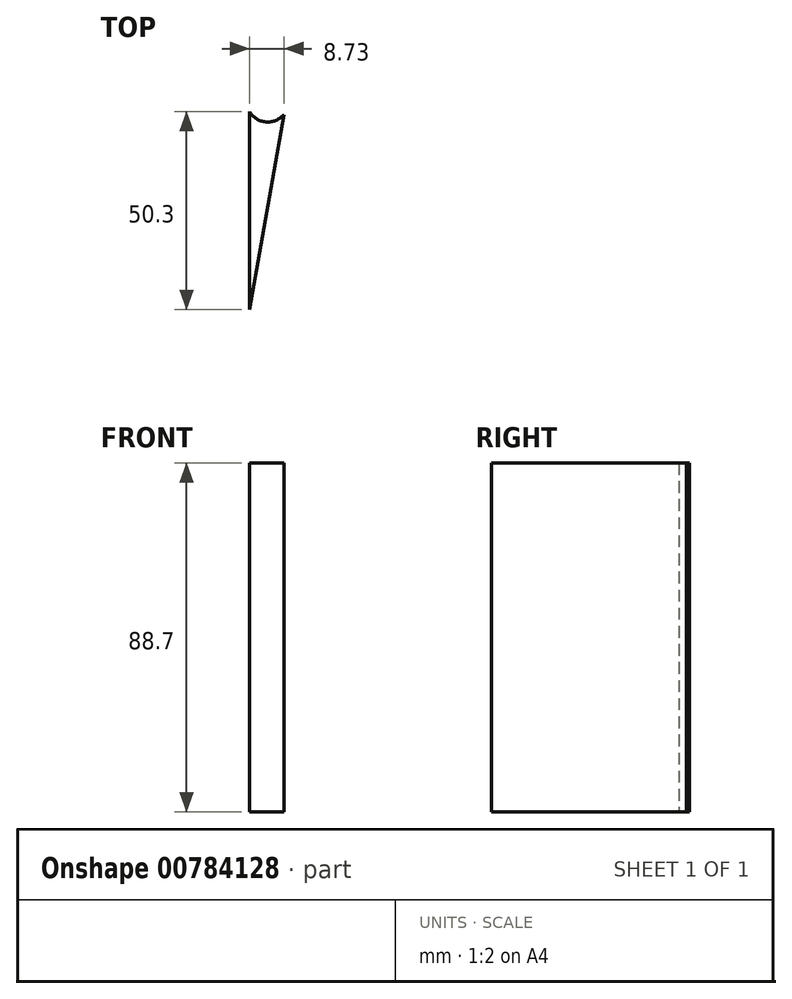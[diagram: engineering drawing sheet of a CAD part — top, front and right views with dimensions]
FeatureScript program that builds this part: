
annotation { "Feature Type Name" : "Feature", "Feature Type Description" : "" }
export const myFeature = defineFeature(function(context is Context, id is Id, definition is map)
    precondition{}
    {
        {
            var Q0;
            Q0=qCreatedBy(makeId("Top.planeOp"),FACE);
            var sketch = newSketch(context, id + "F0", { "sketchPlane" : qUnion([Q0])});
            skArc(sketch, "E0", {"start": v(0, 50.3) * mm, "mid": v(4.17, 47.65) * mm, "end": v(8.73, 49.53) * mm});
            skLineSegment(sketch, "E1", {"start": v(0, 50.3) * mm, "end": v(0, 0) * mm});
            skLineSegment(sketch, "E2", {"start": v(0, 0) * mm, "end": v(8.73, 49.53) * mm});
            skSolve(sketch);
        }
        {
            var Q0;
            Q0=qCreatedBy(makeId("Front.planeOp"),FACE);
            var sketch = newSketch(context, id + "F1", { "sketchPlane" : qUnion([Q0])});
            skLineSegment(sketch, "E3", {"start": v(0, 0) * mm, "end": v(0, 40.63) * mm});
            skSolve(sketch);
        }
        {
            var Q0;
            Q0=makeQuery(id+"FnWcQ6zkBOcur6w_0.24.F0.imprint","IMPRINT",FACE,{"disambiguationData":[TD([[makeQuery(id+"FnWcQ6zkBOcur6w_0.24.F0.imprint","IMPRINT",EDGE,{"derivedFrom":sQuery(id+"FnWcQ6zkBOcur6w_0.24.F0.wireOp",EDGE,"E0")}),-1.0]])]});
            var Q1;
            Q1=makeQuery(id+"FnWcQ6zkBOcur6w_0.16.F0.imprint","IMPRINT",FACE,{"disambiguationData":[TD([[makeQuery(id+"FnWcQ6zkBOcur6w_0.16.F0.imprint","IMPRINT",EDGE,{"derivedFrom":sQuery(id+"FnWcQ6zkBOcur6w_0.16.F0.wireOp",EDGE,"E0")}),-1.0]])]});
            var Q2;
            Q2=makeQuery(id+"FnWcQ6zkBOcur6w_0.19.F0.imprint","IMPRINT",FACE,{"disambiguationData":[TD([[makeQuery(id+"FnWcQ6zkBOcur6w_0.19.F0.imprint","IMPRINT",EDGE,{"derivedFrom":sQuery(id+"FnWcQ6zkBOcur6w_0.19.F0.wireOp",EDGE,"E0")}),-1.0]])]});
            var Q3;
            Q3=makeQuery(id+"FnWcQ6zkBOcur6w_0.-10.F0.imprint","IMPRINT",FACE,{"disambiguationData":[TD([[makeQuery(id+"FnWcQ6zkBOcur6w_0.-10.F0.imprint","IMPRINT",EDGE,{"derivedFrom":sQuery(id+"FnWcQ6zkBOcur6w_0.-10.F0.wireOp",EDGE,"E0")}),-1.0]])]});
            var Q4;
            Q4=makeQuery(id+"FnWcQ6zkBOcur6w_0.11.F0.imprint","IMPRINT",FACE,{"disambiguationData":[TD([[makeQuery(id+"FnWcQ6zkBOcur6w_0.11.F0.imprint","IMPRINT",EDGE,{"derivedFrom":sQuery(id+"FnWcQ6zkBOcur6w_0.11.F0.wireOp",EDGE,"E0")}),-1.0]])]});
            var Q5;
            Q5=makeQuery(id+"FnWcQ6zkBOcur6w_0.-20.F0.imprint","IMPRINT",FACE,{"disambiguationData":[TD([[makeQuery(id+"FnWcQ6zkBOcur6w_0.-20.F0.imprint","IMPRINT",EDGE,{"derivedFrom":sQuery(id+"FnWcQ6zkBOcur6w_0.-20.F0.wireOp",EDGE,"E0")}),-1.0]])]});
            var Q6;
            Q6=makeQuery(id+"FnWcQ6zkBOcur6w_0.-13.F0.imprint","IMPRINT",FACE,{"disambiguationData":[TD([[makeQuery(id+"FnWcQ6zkBOcur6w_0.-13.F0.imprint","IMPRINT",EDGE,{"derivedFrom":sQuery(id+"FnWcQ6zkBOcur6w_0.-13.F0.wireOp",EDGE,"E0")}),-1.0]])]});
            var Q7;
            Q7=makeQuery(id+"FnWcQ6zkBOcur6w_0.-17.F0.imprint","IMPRINT",FACE,{"disambiguationData":[TD([[makeQuery(id+"FnWcQ6zkBOcur6w_0.-17.F0.imprint","IMPRINT",EDGE,{"derivedFrom":sQuery(id+"FnWcQ6zkBOcur6w_0.-17.F0.wireOp",EDGE,"E0")}),-1.0]])]});
            var Q8;
            Q8=makeQuery(id+"FnWcQ6zkBOcur6w_0.-8.F0.imprint","IMPRINT",FACE,{"disambiguationData":[TD([[makeQuery(id+"FnWcQ6zkBOcur6w_0.-8.F0.imprint","IMPRINT",EDGE,{"derivedFrom":sQuery(id+"FnWcQ6zkBOcur6w_0.-8.F0.wireOp",EDGE,"E0")}),-1.0]])]});
            var Q9;
            Q9=makeQuery(id+"FnWcQ6zkBOcur6w_0.20.F0.imprint","IMPRINT",FACE,{"disambiguationData":[TD([[makeQuery(id+"FnWcQ6zkBOcur6w_0.20.F0.imprint","IMPRINT",EDGE,{"derivedFrom":sQuery(id+"FnWcQ6zkBOcur6w_0.20.F0.wireOp",EDGE,"E0")}),-1.0]])]});
            var Q10;
            Q10=makeQuery(id+"FnWcQ6zkBOcur6w_0.-16.F0.imprint","IMPRINT",FACE,{"disambiguationData":[TD([[makeQuery(id+"FnWcQ6zkBOcur6w_0.-16.F0.imprint","IMPRINT",EDGE,{"derivedFrom":sQuery(id+"FnWcQ6zkBOcur6w_0.-16.F0.wireOp",EDGE,"E0")}),-1.0]])]});
            var Q11;
            Q11=makeQuery(id+"FnWcQ6zkBOcur6w_0.12.F0.imprint","IMPRINT",FACE,{"disambiguationData":[TD([[makeQuery(id+"FnWcQ6zkBOcur6w_0.12.F0.imprint","IMPRINT",EDGE,{"derivedFrom":sQuery(id+"FnWcQ6zkBOcur6w_0.12.F0.wireOp",EDGE,"E0")}),-1.0]])]});
            var Q12;
            Q12=makeQuery(id+"FnWcQ6zkBOcur6w_0.25.F0.imprint","IMPRINT",FACE,{"disambiguationData":[TD([[makeQuery(id+"FnWcQ6zkBOcur6w_0.25.F0.imprint","IMPRINT",EDGE,{"derivedFrom":sQuery(id+"FnWcQ6zkBOcur6w_0.25.F0.wireOp",EDGE,"E0")}),-1.0]])]});
            var Q13;
            Q13=makeQuery(id+"FnWcQ6zkBOcur6w_0.-9.F0.imprint","IMPRINT",FACE,{"disambiguationData":[TD([[makeQuery(id+"FnWcQ6zkBOcur6w_0.-9.F0.imprint","IMPRINT",EDGE,{"derivedFrom":sQuery(id+"FnWcQ6zkBOcur6w_0.-9.F0.wireOp",EDGE,"E0")}),-1.0]])]});
            var Q14;
            Q14=makeQuery(id+"FnWcQ6zkBOcur6w_0.-12.F0.imprint","IMPRINT",FACE,{"disambiguationData":[TD([[makeQuery(id+"FnWcQ6zkBOcur6w_0.-12.F0.imprint","IMPRINT",EDGE,{"derivedFrom":sQuery(id+"FnWcQ6zkBOcur6w_0.-12.F0.wireOp",EDGE,"E0")}),-1.0]])]});
            var Q15;
            Q15=makeQuery(id+"FnWcQ6zkBOcur6w_0.-15.F0.imprint","IMPRINT",FACE,{"disambiguationData":[TD([[makeQuery(id+"FnWcQ6zkBOcur6w_0.-15.F0.imprint","IMPRINT",EDGE,{"derivedFrom":sQuery(id+"FnWcQ6zkBOcur6w_0.-15.F0.wireOp",EDGE,"E0")}),-1.0]])]});
            var Q16;
            Q16=makeQuery(id+"FnWcQ6zkBOcur6w_0.13.F0.imprint","IMPRINT",FACE,{"disambiguationData":[TD([[makeQuery(id+"FnWcQ6zkBOcur6w_0.13.F0.imprint","IMPRINT",EDGE,{"derivedFrom":sQuery(id+"FnWcQ6zkBOcur6w_0.13.F0.wireOp",EDGE,"E0")}),-1.0]])]});
            var Q17;
            Q17=makeQuery(id+"FnWcQ6zkBOcur6w_0.26.F0.imprint","IMPRINT",FACE,{"disambiguationData":[TD([[makeQuery(id+"FnWcQ6zkBOcur6w_0.26.F0.imprint","IMPRINT",EDGE,{"derivedFrom":sQuery(id+"FnWcQ6zkBOcur6w_0.26.F0.wireOp",EDGE,"E0")}),-1.0]])]});
            var Q18;
            Q18=makeQuery(id+"FnWcQ6zkBOcur6w_0.-21.F0.imprint","IMPRINT",FACE,{"disambiguationData":[TD([[makeQuery(id+"FnWcQ6zkBOcur6w_0.-21.F0.imprint","IMPRINT",EDGE,{"derivedFrom":sQuery(id+"FnWcQ6zkBOcur6w_0.-21.F0.wireOp",EDGE,"E0")}),-1.0]])]});
            var Q19;
            Q19=makeQuery(id+"FnWcQ6zkBOcur6w_0.-22.F0.imprint","IMPRINT",FACE,{"disambiguationData":[TD([[makeQuery(id+"FnWcQ6zkBOcur6w_0.-22.F0.imprint","IMPRINT",EDGE,{"derivedFrom":sQuery(id+"FnWcQ6zkBOcur6w_0.-22.F0.wireOp",EDGE,"E0")}),-1.0]])]});
            var Q20;
            Q20=makeQuery(id+"FnWcQ6zkBOcur6w_0.18.F0.imprint","IMPRINT",FACE,{"disambiguationData":[TD([[makeQuery(id+"FnWcQ6zkBOcur6w_0.18.F0.imprint","IMPRINT",EDGE,{"derivedFrom":sQuery(id+"FnWcQ6zkBOcur6w_0.18.F0.wireOp",EDGE,"E0")}),-1.0]])]});
            var Q21;
            Q21=makeQuery(id+"FnWcQ6zkBOcur6w_0.-23.F0.imprint","IMPRINT",FACE,{"disambiguationData":[TD([[makeQuery(id+"FnWcQ6zkBOcur6w_0.-23.F0.imprint","IMPRINT",EDGE,{"derivedFrom":sQuery(id+"FnWcQ6zkBOcur6w_0.-23.F0.wireOp",EDGE,"E0")}),-1.0]])]});
            var Q22;
            Q22=makeQuery(id+"FnWcQ6zkBOcur6w_0.-24.F0.imprint","IMPRINT",FACE,{"disambiguationData":[TD([[makeQuery(id+"FnWcQ6zkBOcur6w_0.-24.F0.imprint","IMPRINT",EDGE,{"derivedFrom":sQuery(id+"FnWcQ6zkBOcur6w_0.-24.F0.wireOp",EDGE,"E0")}),-1.0]])]});
            var Q23;
            Q23=makeQuery(id+"FnWcQ6zkBOcur6w_0.10.F0.imprint","IMPRINT",FACE,{"disambiguationData":[TD([[makeQuery(id+"FnWcQ6zkBOcur6w_0.10.F0.imprint","IMPRINT",EDGE,{"derivedFrom":sQuery(id+"FnWcQ6zkBOcur6w_0.10.F0.wireOp",EDGE,"E0")}),-1.0]])]});
            var Q24;
            Q24=makeQuery(id+"FnWcQ6zkBOcur6w_0.-25.F0.imprint","IMPRINT",FACE,{"disambiguationData":[TD([[makeQuery(id+"FnWcQ6zkBOcur6w_0.-25.F0.imprint","IMPRINT",EDGE,{"derivedFrom":sQuery(id+"FnWcQ6zkBOcur6w_0.-25.F0.wireOp",EDGE,"E0")}),-1.0]])]});
            var Q25;
            Q25=makeQuery(id+"FnWcQ6zkBOcur6w_0.-26.F0.imprint","IMPRINT",FACE,{"disambiguationData":[TD([[makeQuery(id+"FnWcQ6zkBOcur6w_0.-26.F0.imprint","IMPRINT",EDGE,{"derivedFrom":sQuery(id+"FnWcQ6zkBOcur6w_0.-26.F0.wireOp",EDGE,"E0")}),-1.0]])]});
            var Q26;
            Q26=makeQuery(id+"FnWcQ6zkBOcur6w_0.23.F0.imprint","IMPRINT",FACE,{"disambiguationData":[TD([[makeQuery(id+"FnWcQ6zkBOcur6w_0.23.F0.imprint","IMPRINT",EDGE,{"derivedFrom":sQuery(id+"FnWcQ6zkBOcur6w_0.23.F0.wireOp",EDGE,"E0")}),-1.0]])]});
            var Q27;
            Q27=makeQuery(id+"FnWcQ6zkBOcur6w_0.27.F0.imprint","IMPRINT",FACE,{"disambiguationData":[TD([[makeQuery(id+"FnWcQ6zkBOcur6w_0.27.F0.imprint","IMPRINT",EDGE,{"derivedFrom":sQuery(id+"FnWcQ6zkBOcur6w_0.27.F0.wireOp",EDGE,"E0")}),-1.0]])]});
            var Q28;
            Q28=makeQuery(id+"FnWcQ6zkBOcur6w_0.-11.F0.imprint","IMPRINT",FACE,{"disambiguationData":[TD([[makeQuery(id+"FnWcQ6zkBOcur6w_0.-11.F0.imprint","IMPRINT",EDGE,{"derivedFrom":sQuery(id+"FnWcQ6zkBOcur6w_0.-11.F0.wireOp",EDGE,"E0")}),-1.0]])]});
            var Q29;
            Q29=makeQuery(id+"FnWcQ6zkBOcur6w_0.15.F0.imprint","IMPRINT",FACE,{"disambiguationData":[TD([[makeQuery(id+"FnWcQ6zkBOcur6w_0.15.F0.imprint","IMPRINT",EDGE,{"derivedFrom":sQuery(id+"FnWcQ6zkBOcur6w_0.15.F0.wireOp",EDGE,"E0")}),-1.0]])]});
            var Q30;
            Q30=makeQuery(id+"FnWcQ6zkBOcur6w_0.-14.F0.imprint","IMPRINT",FACE,{"disambiguationData":[TD([[makeQuery(id+"FnWcQ6zkBOcur6w_0.-14.F0.imprint","IMPRINT",EDGE,{"derivedFrom":sQuery(id+"FnWcQ6zkBOcur6w_0.-14.F0.wireOp",EDGE,"E0")}),-1.0]])]});
            var Q31;
            Q31=makeQuery(id+"FnWcQ6zkBOcur6w_0.14.F0.imprint","IMPRINT",FACE,{"disambiguationData":[TD([[makeQuery(id+"FnWcQ6zkBOcur6w_0.14.F0.imprint","IMPRINT",EDGE,{"derivedFrom":sQuery(id+"FnWcQ6zkBOcur6w_0.14.F0.wireOp",EDGE,"E0")}),-1.0]])]});
            var Q32;
            Q32=makeQuery(id+"FnWcQ6zkBOcur6w_0.-18.F0.imprint","IMPRINT",FACE,{"disambiguationData":[TD([[makeQuery(id+"FnWcQ6zkBOcur6w_0.-18.F0.imprint","IMPRINT",EDGE,{"derivedFrom":sQuery(id+"FnWcQ6zkBOcur6w_0.-18.F0.wireOp",EDGE,"E0")}),-1.0]])]});
            var Q33;
            Q33=makeQuery(id+"FnWcQ6zkBOcur6w_0.28.F0.imprint","IMPRINT",FACE,{"disambiguationData":[TD([[makeQuery(id+"FnWcQ6zkBOcur6w_0.28.F0.imprint","IMPRINT",EDGE,{"derivedFrom":sQuery(id+"FnWcQ6zkBOcur6w_0.28.F0.wireOp",EDGE,"E0")}),-1.0]])]});
            var Q34;
            Q34=makeQuery(id+"FnWcQ6zkBOcur6w_0.4.F0.imprint","IMPRINT",FACE,{"disambiguationData":[TD([[makeQuery(id+"FnWcQ6zkBOcur6w_0.4.F0.imprint","IMPRINT",EDGE,{"derivedFrom":sQuery(id+"FnWcQ6zkBOcur6w_0.4.F0.wireOp",EDGE,"E0")}),-1.0]])]});
            var Q35;
            Q35=makeQuery(id+"FnWcQ6zkBOcur6w_0.-33.F0.imprint","IMPRINT",FACE,{"disambiguationData":[TD([[makeQuery(id+"FnWcQ6zkBOcur6w_0.-33.F0.imprint","IMPRINT",EDGE,{"derivedFrom":sQuery(id+"FnWcQ6zkBOcur6w_0.-33.F0.wireOp",EDGE,"E0")}),-1.0]])]});
            var Q36;
            Q36=makeQuery(id+"FnWcQ6zkBOcur6w_0.-2.F0.imprint","IMPRINT",FACE,{"disambiguationData":[TD([[makeQuery(id+"FnWcQ6zkBOcur6w_0.-2.F0.imprint","IMPRINT",EDGE,{"derivedFrom":sQuery(id+"FnWcQ6zkBOcur6w_0.-2.F0.wireOp",EDGE,"E0")}),-1.0]])]});
            var Q37;
            Q37=makeQuery(id+"FnWcQ6zkBOcur6w_0.35.F0.imprint","IMPRINT",FACE,{"disambiguationData":[TD([[makeQuery(id+"FnWcQ6zkBOcur6w_0.35.F0.imprint","IMPRINT",EDGE,{"derivedFrom":sQuery(id+"FnWcQ6zkBOcur6w_0.35.F0.wireOp",EDGE,"E0")}),-1.0]])]});
            var Q38;
            Q38=makeQuery(id+"FnWcQ6zkBOcur6w_0.8.F0.imprint","IMPRINT",FACE,{"disambiguationData":[TD([[makeQuery(id+"FnWcQ6zkBOcur6w_0.8.F0.imprint","IMPRINT",EDGE,{"derivedFrom":sQuery(id+"FnWcQ6zkBOcur6w_0.8.F0.wireOp",EDGE,"E0")}),-1.0]])]});
            var Q39;
            Q39=makeQuery(id+"FnWcQ6zkBOcur6w_0.-34.F0.imprint","IMPRINT",FACE,{"disambiguationData":[TD([[makeQuery(id+"FnWcQ6zkBOcur6w_0.-34.F0.imprint","IMPRINT",EDGE,{"derivedFrom":sQuery(id+"FnWcQ6zkBOcur6w_0.-34.F0.wireOp",EDGE,"E0")}),-1.0]])]});
            var Q40;
            Q40=makeQuery(id+"FnWcQ6zkBOcur6w_0.-35.F0.imprint","IMPRINT",FACE,{"disambiguationData":[TD([[makeQuery(id+"FnWcQ6zkBOcur6w_0.-35.F0.imprint","IMPRINT",EDGE,{"derivedFrom":sQuery(id+"FnWcQ6zkBOcur6w_0.-35.F0.wireOp",EDGE,"E0")}),-1.0]])]});
            var Q41;
            Q41=makeQuery(id+"FnWcQ6zkBOcur6w_0.-5.F0.imprint","IMPRINT",FACE,{"disambiguationData":[TD([[makeQuery(id+"FnWcQ6zkBOcur6w_0.-5.F0.imprint","IMPRINT",EDGE,{"derivedFrom":sQuery(id+"FnWcQ6zkBOcur6w_0.-5.F0.wireOp",EDGE,"E0")}),-1.0]])]});
            var Q42;
            Q42=makeQuery(id+"FnWcQ6zkBOcur6w_0.32.F0.imprint","IMPRINT",FACE,{"disambiguationData":[TD([[makeQuery(id+"FnWcQ6zkBOcur6w_0.32.F0.imprint","IMPRINT",EDGE,{"derivedFrom":sQuery(id+"FnWcQ6zkBOcur6w_0.32.F0.wireOp",EDGE,"E0")}),-1.0]])]});
            var Q43;
            Q43=makeQuery(id+"FnWcQ6zkBOcur6w_0.-1.F0.imprint","IMPRINT",FACE,{"disambiguationData":[TD([[makeQuery(id+"FnWcQ6zkBOcur6w_0.-1.F0.imprint","IMPRINT",EDGE,{"derivedFrom":sQuery(id+"FnWcQ6zkBOcur6w_0.-1.F0.wireOp",EDGE,"E0")}),-1.0]])]});
            var Q44;
            Q44=makeQuery(id+"FnWcQ6zkBOcur6w_0.29.F0.imprint","IMPRINT",FACE,{"disambiguationData":[TD([[makeQuery(id+"FnWcQ6zkBOcur6w_0.29.F0.imprint","IMPRINT",EDGE,{"derivedFrom":sQuery(id+"FnWcQ6zkBOcur6w_0.29.F0.wireOp",EDGE,"E0")}),-1.0]])]});
            var Q45;
            Q45=makeQuery(id+"FnWcQ6zkBOcur6w_0.17.F0.imprint","IMPRINT",FACE,{"disambiguationData":[TD([[makeQuery(id+"FnWcQ6zkBOcur6w_0.17.F0.imprint","IMPRINT",EDGE,{"derivedFrom":sQuery(id+"FnWcQ6zkBOcur6w_0.17.F0.wireOp",EDGE,"E0")}),-1.0]])]});
            var Q46;
            Q46=makeQuery(id+"FnWcQ6zkBOcur6w_0.-4.F0.imprint","IMPRINT",FACE,{"disambiguationData":[TD([[makeQuery(id+"FnWcQ6zkBOcur6w_0.-4.F0.imprint","IMPRINT",EDGE,{"derivedFrom":sQuery(id+"FnWcQ6zkBOcur6w_0.-4.F0.wireOp",EDGE,"E0")}),-1.0]])]});
            var Q47;
            Q47=makeQuery(id+"FnWcQ6zkBOcur6w_0.33.F0.imprint","IMPRINT",FACE,{"disambiguationData":[TD([[makeQuery(id+"FnWcQ6zkBOcur6w_0.33.F0.imprint","IMPRINT",EDGE,{"derivedFrom":sQuery(id+"FnWcQ6zkBOcur6w_0.33.F0.wireOp",EDGE,"E0")}),-1.0]])]});
            var Q48;
            Q48=makeQuery(id+"FnWcQ6zkBOcur6w_0.2.F0.imprint","IMPRINT",FACE,{"disambiguationData":[TD([[makeQuery(id+"FnWcQ6zkBOcur6w_0.2.F0.imprint","IMPRINT",EDGE,{"derivedFrom":sQuery(id+"FnWcQ6zkBOcur6w_0.2.F0.wireOp",EDGE,"E0")}),-1.0]])]});
            var Q49;
            Q49=makeQuery(id+"FnWcQ6zkBOcur6w_0.-7.F0.imprint","IMPRINT",FACE,{"disambiguationData":[TD([[makeQuery(id+"FnWcQ6zkBOcur6w_0.-7.F0.imprint","IMPRINT",EDGE,{"derivedFrom":sQuery(id+"FnWcQ6zkBOcur6w_0.-7.F0.wireOp",EDGE,"E0")}),-1.0]])]});
            var Q50;
            Q50=makeQuery(id+"FnWcQ6zkBOcur6w_0.21.F0.imprint","IMPRINT",FACE,{"disambiguationData":[TD([[makeQuery(id+"FnWcQ6zkBOcur6w_0.21.F0.imprint","IMPRINT",EDGE,{"derivedFrom":sQuery(id+"FnWcQ6zkBOcur6w_0.21.F0.wireOp",EDGE,"E0")}),-1.0]])]});
            var Q51;
            Q51=makeQuery(id+"FnWcQ6zkBOcur6w_0.1.F0.imprint","IMPRINT",FACE,{"disambiguationData":[TD([[makeQuery(id+"FnWcQ6zkBOcur6w_0.1.F0.imprint","IMPRINT",EDGE,{"derivedFrom":sQuery(id+"FnWcQ6zkBOcur6w_0.1.F0.wireOp",EDGE,"E0")}),-1.0]])]});
            var Q52;
            Q52=makeQuery(id+"FnWcQ6zkBOcur6w_0.-3.F0.imprint","IMPRINT",FACE,{"disambiguationData":[TD([[makeQuery(id+"FnWcQ6zkBOcur6w_0.-3.F0.imprint","IMPRINT",EDGE,{"derivedFrom":sQuery(id+"FnWcQ6zkBOcur6w_0.-3.F0.wireOp",EDGE,"E0")}),-1.0]])]});
            var Q53;
            Q53=makeQuery(id+"FnWcQ6zkBOcur6w_0.-27.F0.imprint","IMPRINT",FACE,{"disambiguationData":[TD([[makeQuery(id+"FnWcQ6zkBOcur6w_0.-27.F0.imprint","IMPRINT",EDGE,{"derivedFrom":sQuery(id+"FnWcQ6zkBOcur6w_0.-27.F0.wireOp",EDGE,"E0")}),-1.0]])]});
            var Q54;
            Q54=makeQuery(id+"FnWcQ6zkBOcur6w_0.-28.F0.imprint","IMPRINT",FACE,{"disambiguationData":[TD([[makeQuery(id+"FnWcQ6zkBOcur6w_0.-28.F0.imprint","IMPRINT",EDGE,{"derivedFrom":sQuery(id+"FnWcQ6zkBOcur6w_0.-28.F0.wireOp",EDGE,"E0")}),-1.0]])]});
            var Q55;
            Q55=makeQuery(id+"FnWcQ6zkBOcur6w_0.7.F0.imprint","IMPRINT",FACE,{"disambiguationData":[TD([[makeQuery(id+"FnWcQ6zkBOcur6w_0.7.F0.imprint","IMPRINT",EDGE,{"derivedFrom":sQuery(id+"FnWcQ6zkBOcur6w_0.7.F0.wireOp",EDGE,"E0")}),-1.0]])]});
            var Q56;
            Q56=makeQuery(id+"FnWcQ6zkBOcur6w_0.-29.F0.imprint","IMPRINT",FACE,{"disambiguationData":[TD([[makeQuery(id+"FnWcQ6zkBOcur6w_0.-29.F0.imprint","IMPRINT",EDGE,{"derivedFrom":sQuery(id+"FnWcQ6zkBOcur6w_0.-29.F0.wireOp",EDGE,"E0")}),-1.0]])]});
            var Q57;
            Q57=makeQuery(id+"FnWcQ6zkBOcur6w_0.34.F0.imprint","IMPRINT",FACE,{"disambiguationData":[TD([[makeQuery(id+"FnWcQ6zkBOcur6w_0.34.F0.imprint","IMPRINT",EDGE,{"derivedFrom":sQuery(id+"FnWcQ6zkBOcur6w_0.34.F0.wireOp",EDGE,"E0")}),-1.0]])]});
            var Q58;
            Q58=makeQuery(id+"FnWcQ6zkBOcur6w_0.3.F0.imprint","IMPRINT",FACE,{"disambiguationData":[TD([[makeQuery(id+"FnWcQ6zkBOcur6w_0.3.F0.imprint","IMPRINT",EDGE,{"derivedFrom":sQuery(id+"FnWcQ6zkBOcur6w_0.3.F0.wireOp",EDGE,"E0")}),-1.0]])]});
            var Q59;
            Q59=makeQuery(id+"F0.imprint","IMPRINT",FACE,{"disambiguationData":[TD([[makeQuery(id+"F0.imprint","IMPRINT",EDGE,{"derivedFrom":sQuery(id+"F0.wireOp",EDGE,"E0")}),-1.0]])]});
            var Q60;
            Q60=makeQuery(id+"FnWcQ6zkBOcur6w_0.-6.F0.imprint","IMPRINT",FACE,{"disambiguationData":[TD([[makeQuery(id+"FnWcQ6zkBOcur6w_0.-6.F0.imprint","IMPRINT",EDGE,{"derivedFrom":sQuery(id+"FnWcQ6zkBOcur6w_0.-6.F0.wireOp",EDGE,"E0")}),-1.0]])]});
            var Q61;
            Q61=makeQuery(id+"FnWcQ6zkBOcur6w_0.22.F0.imprint","IMPRINT",FACE,{"disambiguationData":[TD([[makeQuery(id+"FnWcQ6zkBOcur6w_0.22.F0.imprint","IMPRINT",EDGE,{"derivedFrom":sQuery(id+"FnWcQ6zkBOcur6w_0.22.F0.wireOp",EDGE,"E0")}),-1.0]])]});
            var Q62;
            Q62=makeQuery(id+"FnWcQ6zkBOcur6w_0.-30.F0.imprint","IMPRINT",FACE,{"disambiguationData":[TD([[makeQuery(id+"FnWcQ6zkBOcur6w_0.-30.F0.imprint","IMPRINT",EDGE,{"derivedFrom":sQuery(id+"FnWcQ6zkBOcur6w_0.-30.F0.wireOp",EDGE,"E0")}),-1.0]])]});
            var Q63;
            Q63=makeQuery(id+"FnWcQ6zkBOcur6w_0.-31.F0.imprint","IMPRINT",FACE,{"disambiguationData":[TD([[makeQuery(id+"FnWcQ6zkBOcur6w_0.-31.F0.imprint","IMPRINT",EDGE,{"derivedFrom":sQuery(id+"FnWcQ6zkBOcur6w_0.-31.F0.wireOp",EDGE,"E0")}),-1.0]])]});
            var Q64;
            Q64=makeQuery(id+"FnWcQ6zkBOcur6w_0.5.F0.imprint","IMPRINT",FACE,{"disambiguationData":[TD([[makeQuery(id+"FnWcQ6zkBOcur6w_0.5.F0.imprint","IMPRINT",EDGE,{"derivedFrom":sQuery(id+"FnWcQ6zkBOcur6w_0.5.F0.wireOp",EDGE,"E0")}),-1.0]])]});
            var Q65;
            Q65=makeQuery(id+"FnWcQ6zkBOcur6w_0.-32.F0.imprint","IMPRINT",FACE,{"disambiguationData":[TD([[makeQuery(id+"FnWcQ6zkBOcur6w_0.-32.F0.imprint","IMPRINT",EDGE,{"derivedFrom":sQuery(id+"FnWcQ6zkBOcur6w_0.-32.F0.wireOp",EDGE,"E0")}),-1.0]])]});
            var Q66;
            Q66=makeQuery(id+"FnWcQ6zkBOcur6w_0.31.F0.imprint","IMPRINT",FACE,{"disambiguationData":[TD([[makeQuery(id+"FnWcQ6zkBOcur6w_0.31.F0.imprint","IMPRINT",EDGE,{"derivedFrom":sQuery(id+"FnWcQ6zkBOcur6w_0.31.F0.wireOp",EDGE,"E0")}),-1.0]])]});
            var Q67;
            Q67=makeQuery(id+"FnWcQ6zkBOcur6w_0.-19.F0.imprint","IMPRINT",FACE,{"disambiguationData":[TD([[makeQuery(id+"FnWcQ6zkBOcur6w_0.-19.F0.imprint","IMPRINT",EDGE,{"derivedFrom":sQuery(id+"FnWcQ6zkBOcur6w_0.-19.F0.wireOp",EDGE,"E0")}),-1.0]])]});
            var Q68;
            Q68=makeQuery(id+"FnWcQ6zkBOcur6w_0.9.F0.imprint","IMPRINT",FACE,{"disambiguationData":[TD([[makeQuery(id+"FnWcQ6zkBOcur6w_0.9.F0.imprint","IMPRINT",EDGE,{"derivedFrom":sQuery(id+"FnWcQ6zkBOcur6w_0.9.F0.wireOp",EDGE,"E0")}),-1.0]])]});
            var Q69;
            Q69=makeQuery(id+"FnWcQ6zkBOcur6w_0.6.F0.imprint","IMPRINT",FACE,{"disambiguationData":[TD([[makeQuery(id+"FnWcQ6zkBOcur6w_0.6.F0.imprint","IMPRINT",EDGE,{"derivedFrom":sQuery(id+"FnWcQ6zkBOcur6w_0.6.F0.wireOp",EDGE,"E0")}),-1.0]])]});
            var Q70;
            Q70=makeQuery(id+"FnWcQ6zkBOcur6w_0.30.F0.imprint","IMPRINT",FACE,{"disambiguationData":[TD([[makeQuery(id+"FnWcQ6zkBOcur6w_0.30.F0.imprint","IMPRINT",EDGE,{"derivedFrom":sQuery(id+"FnWcQ6zkBOcur6w_0.30.F0.wireOp",EDGE,"E0")}),-1.0]])]});
            extrude(context, id + "F2", {"entities" : qUnion([Q0, Q1, Q2, Q3, Q4, Q5, Q6, Q7, Q8, Q9, Q10, Q11, Q12, Q13, Q14, Q15, Q16, Q17, Q18, Q19, Q20, Q21, Q22, Q23, Q24, Q25, Q26, Q27, Q28, Q29, Q30, Q31, Q32, Q33, Q34, Q35, Q36, Q37, Q38, Q39, Q40, Q41, Q42, Q43, Q44, Q45, Q46, Q47, Q48, Q49, Q50, Q51, Q52, Q53, Q54, Q55, Q56, Q57, Q58, Q59, Q60, Q61, Q62, Q63, Q64, Q65, Q66, Q67, Q68, Q69, Q70]), "depth" : 88.7 * mm, "offsetDistance" : 25 * mm});
        }
    });
